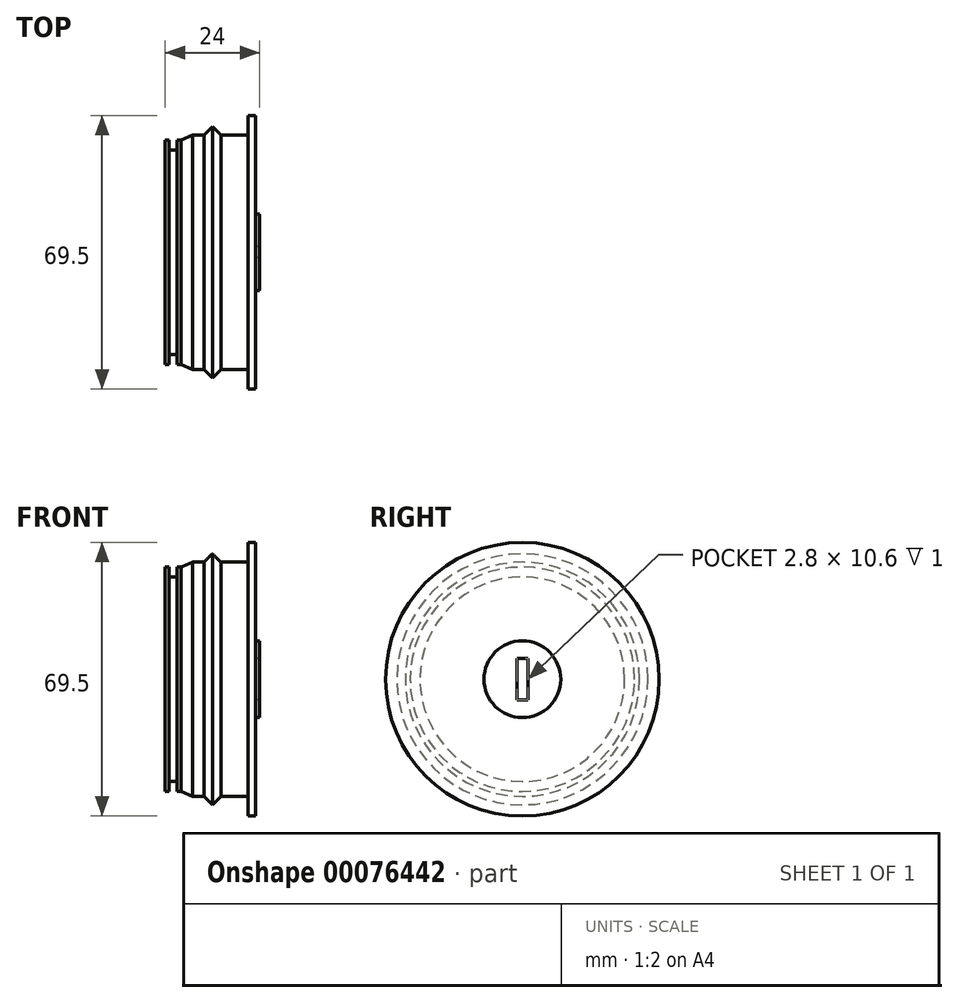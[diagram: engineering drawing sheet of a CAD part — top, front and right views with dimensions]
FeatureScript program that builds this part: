
annotation { "Feature Type Name" : "Feature", "Feature Type Description" : "" }
export const myFeature = defineFeature(function(context is Context, id is Id, definition is map)
    precondition{}
    {
        {
            var Q0;
            Q0=qCreatedBy(makeId("Front.planeOp"),FACE);
            var sketch = newSketch(context, id + "F0", { "sketchPlane" : qUnion([Q0])});
            skLineSegment(sketch, "E0", {"start": v(-21.4, 0) * mm, "end": v(22.1, 0) * mm, "construction": true});
            skLineSegment(sketch, "E1", {"start": v(0, 0) * mm, "end": v(0, 28.5) * mm});
            skLineSegment(sketch, "E2", {"start": v(0, 28.5) * mm, "end": v(1, 28.5) * mm});
            skLineSegment(sketch, "E3", {"start": v(1, 28.5) * mm, "end": v(1, 26) * mm});
            skLineSegment(sketch, "E4", {"start": v(1, 26) * mm, "end": v(3, 26) * mm});
            skLineSegment(sketch, "E5", {"start": v(3, 26) * mm, "end": v(3, 28.5) * mm});
            skLineSegment(sketch, "E6", {"start": v(3, 28.5) * mm, "end": v(4, 28.5) * mm});
            skLineSegment(sketch, "E7", {"start": v(4, 28.5) * mm, "end": v(7, 29.75) * mm});
            skLineSegment(sketch, "E8", {"start": v(7, 29.75) * mm, "end": v(9.85, 29.75) * mm});
            skLineSegment(sketch, "E9", {"start": v(9.85, 29.75) * mm, "end": v(12, 31.9) * mm});
            skLineSegment(sketch, "E10", {"start": v(12, 31.9) * mm, "end": v(14.15, 29.75) * mm});
            skLineSegment(sketch, "E11", {"start": v(14.15, 29.75) * mm, "end": v(21, 29.75) * mm});
            skLineSegment(sketch, "E12", {"start": v(21, 29.75) * mm, "end": v(21, 34.75) * mm});
            skLineSegment(sketch, "E13", {"start": v(21, 34.75) * mm, "end": v(23, 34.75) * mm});
            skLineSegment(sketch, "E14", {"start": v(23, 34.75) * mm, "end": v(23, 0) * mm});
            skLineSegment(sketch, "E15", {"start": v(0, 0) * mm, "end": v(23, 0) * mm});
            skSolve(sketch);
        }
        {
            var Q0;
            Q0 = qSketchRegion(id + "F0", true);
            var Q1;
            Q1=sQuery(id+"F0.wireOp",EDGE,"E0");
            revolve(context, id + "F1", {"entities" : qUnion([Q0]), "axis" : qUnion([Q1]), "revolveType" : RevolveType.FULL});
        }
        {
            var Q0;
            Q0=makeQuery(id+"F1.opRevolve","SWEPT_FACE",FACE,{"disambiguationData":[OSD([sQuery(id+"F0.wireOp",EDGE,"E14")])]});
            var sketch = newSketch(context, id + "F2", { "sketchPlane" : qUnion([Q0])});
            skCircle(sketch, "E16", {"center": v(0, 0) * mm, "radius": 9.75 * mm});
            skLineSegment(sketch, "E17.bottom", {"start": v(1.4, 5.3) * mm, "end": v(-1.4, 5.3) * mm});
            skLineSegment(sketch, "E17.top", {"start": v(1.4, -5.3) * mm, "end": v(-1.4, -5.3) * mm});
            skLineSegment(sketch, "E17.left", {"start": v(1.4, 5.3) * mm, "end": v(1.4, -5.3) * mm});
            skLineSegment(sketch, "E17.right", {"start": v(-1.4, 5.3) * mm, "end": v(-1.4, -5.3) * mm});
            skSolve(sketch);
        }
        {
            var Q0;
            Q0=makeQuery(id+"F2.imprint","IMPRINT",FACE,{"disambiguationData":[TD([[makeQuery(id+"F2.imprint","IMPRINT",EDGE,{"derivedFrom":sQuery(id+"F2.wireOp",EDGE,"E16")}),1.0]])]});
            extrude(context, id + "F3", {"entities" : qUnion([Q0]), "operationType" : NewBodyOperationType.ADD, "depth" : 1 * mm});
        }
    });
